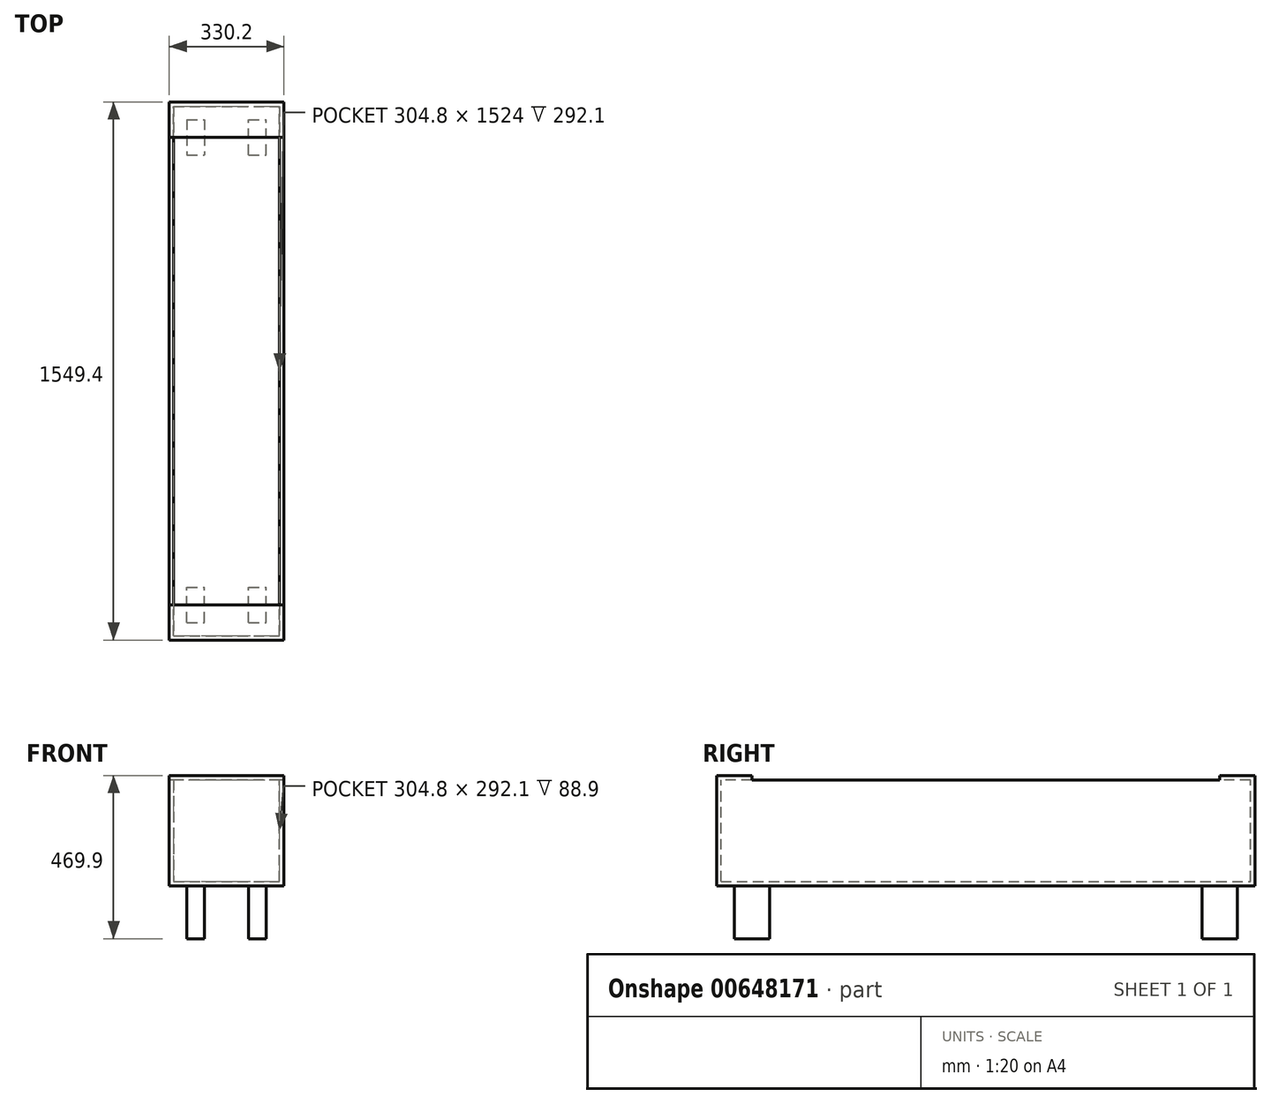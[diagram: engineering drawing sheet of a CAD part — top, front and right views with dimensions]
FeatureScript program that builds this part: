
annotation { "Feature Type Name" : "Feature", "Feature Type Description" : "" }
export const myFeature = defineFeature(function(context is Context, id is Id, definition is map)
    precondition{}
    {
        {
            var Q0;
            Q0=qCreatedBy(makeId("Front.planeOp"),FACE);
            var sketch = newSketch(context, id + "F0", { "sketchPlane" : qUnion([Q0])});
            skLineSegment(sketch, "E0.bottom", {"start": v(-260.83, -10.7) * mm, "end": v(43.97, -10.7) * mm});
            skLineSegment(sketch, "E0.top", {"start": v(-260.83, -23.4) * mm, "end": v(43.97, -23.4) * mm});
            skLineSegment(sketch, "E0.left", {"start": v(-260.83, -10.7) * mm, "end": v(-260.83, -23.4) * mm});
            skLineSegment(sketch, "E0.right", {"start": v(43.97, -10.7) * mm, "end": v(43.97, -23.4) * mm});
            skSolve(sketch);
        }
        {
            var Q0;
            Q0=makeQuery(id+"F0.imprint","IMPRINT",FACE,{"disambiguationData":[TD([[makeQuery(id+"F0.imprint","IMPRINT",EDGE,{"derivedFrom":sQuery(id+"F0.wireOp",EDGE,"E0.bottom")}),-1.0]])]});
            extrude(context, id + "F1", {"entities" : qUnion([Q0]), "depth" : 1524 * mm, "offsetDistance" : 25.4 * mm});
        }
        {
            var Q0;
            Q0=makeQuery(id+"F1.opExtrude","CAP_FACE",FACE,{"disambiguationData":[OSD([sQuery(id+"F0.wireOp",EDGE,"E0.bottom"),sQuery(id+"F0.wireOp",EDGE,"E0.top"),sQuery(id+"F0.wireOp",EDGE,"E0.left"),sQuery(id+"F0.wireOp",EDGE,"E0.right")])],"isStart":false});
            var sketch = newSketch(context, id + "F2", { "sketchPlane" : qUnion([Q0])});
            skLineSegment(sketch, "E1.bottom", {"start": v(43.97, -23.4) * mm, "end": v(56.67, -23.4) * mm});
            skLineSegment(sketch, "E1.top", {"start": v(43.97, 281.4) * mm, "end": v(56.67, 281.4) * mm});
            skLineSegment(sketch, "E1.left", {"start": v(43.97, -23.4) * mm, "end": v(43.97, 281.4) * mm});
            skLineSegment(sketch, "E1.right", {"start": v(56.67, -23.4) * mm, "end": v(56.67, 281.4) * mm});
            skLineSegment(sketch, "E2.bottom", {"start": v(-260.83, -23.4) * mm, "end": v(-273.53, -23.4) * mm});
            skLineSegment(sketch, "E2.top", {"start": v(-260.83, 281.4) * mm, "end": v(-273.53, 281.4) * mm});
            skLineSegment(sketch, "E2.left", {"start": v(-260.83, -23.4) * mm, "end": v(-260.83, 281.4) * mm});
            skLineSegment(sketch, "E2.right", {"start": v(-273.53, -23.4) * mm, "end": v(-273.53, 281.4) * mm});
            skSolve(sketch);
        }
        {
            var Q0;
            {var subQ3=sQuery(id+"F2.wireOp",EDGE,"E2.bottom");Q0=makeQuery(id+"F2.imprint","IMPRINT",FACE,{"disambiguationData":[TD([[makeQuery(id+"F2.imprint","IMPRINT",EDGE,{"derivedFrom":subQ3}),-1.0]])]});}
            var Q1;
            {var subQ2=sQuery(id+"F2.wireOp",EDGE,"E1.bottom");Q1=makeQuery(id+"F2.imprint","IMPRINT",FACE,{"disambiguationData":[TD([[makeQuery(id+"F2.imprint","IMPRINT",EDGE,{"derivedFrom":subQ2}),1.0]])]});}
            extrude(context, id + "F3", {"entities" : qUnion([Q0, Q1]), "operationType" : NewBodyOperationType.ADD, "oppositeDirection" : true, "depth" : 1524 * mm, "offsetDistance" : 25.4 * mm});
        }
        {
            var Q0;
            Q0=makeQuery(id+"F3.opExtrude","SWEPT_FACE",FACE,{"disambiguationData":[OSD([sQuery(id+"F2.wireOp",EDGE,"E2.right")])]});
            var sketch = newSketch(context, id + "F4", { "sketchPlane" : qUnion([Q0])});
            skLineSegment(sketch, "E3.bottom", {"start": v(0, -23.4) * mm, "end": v(-12.7, -23.4) * mm});
            skLineSegment(sketch, "E3.top", {"start": v(0, 281.4) * mm, "end": v(-12.7, 281.4) * mm});
            skLineSegment(sketch, "E3.left", {"start": v(0, -23.4) * mm, "end": v(0, 281.4) * mm});
            skLineSegment(sketch, "E3.right", {"start": v(-12.7, -23.4) * mm, "end": v(-12.7, 281.4) * mm});
            skLineSegment(sketch, "E4.bottom", {"start": v(1524, -23.4) * mm, "end": v(1536.7, -23.4) * mm});
            skLineSegment(sketch, "E4.top", {"start": v(1524, 281.4) * mm, "end": v(1536.7, 281.4) * mm});
            skLineSegment(sketch, "E4.left", {"start": v(1524, -23.4) * mm, "end": v(1524, 281.4) * mm});
            skLineSegment(sketch, "E4.right", {"start": v(1536.7, -23.4) * mm, "end": v(1536.7, 281.4) * mm});
            skSolve(sketch);
        }
        {
            var Q0;
            Q0=makeQuery(id+"F4.imprint","IMPRINT",FACE,{"disambiguationData":[TD([[makeQuery(id+"F4.imprint","IMPRINT",EDGE,{"derivedFrom":sQuery(id+"F4.wireOp",EDGE,"E3.bottom")}),-1.0]])]});
            var Q1;
            Q1=makeQuery(id+"F4.imprint","IMPRINT",FACE,{"disambiguationData":[TD([[makeQuery(id+"F4.imprint","IMPRINT",EDGE,{"derivedFrom":sQuery(id+"F4.wireOp",EDGE,"E4.bottom")}),1.0]])]});
            extrude(context, id + "F5", {"entities" : qUnion([Q0, Q1]), "operationType" : NewBodyOperationType.ADD, "oppositeDirection" : true, "depth" : 330.2 * mm, "offsetDistance" : 25.4 * mm});
        }
        {
            var Q0;
            Q0=makeQuery(id+"F5.boolean.opBoolean","MERGE",FACE,{"derivedFrom":[makeQuery(id+"F3.opExtrude","SWEPT_FACE",FACE,{"disambiguationData":[OSD([sQuery(id+"F2.wireOp",EDGE,"E2.right")])]}),makeQuery(id+"F5.opExtrude","CAP_FACE",FACE,{"disambiguationData":[OSD([sQuery(id+"F4.wireOp",EDGE,"E3.bottom"),sQuery(id+"F4.wireOp",EDGE,"E3.top"),sQuery(id+"F4.wireOp",EDGE,"E3.left"),sQuery(id+"F4.wireOp",EDGE,"E3.right")])],"isStart":true}),makeQuery(id+"F5.opExtrude","CAP_FACE",FACE,{"disambiguationData":[OSD([sQuery(id+"F4.wireOp",EDGE,"E4.bottom"),sQuery(id+"F4.wireOp",EDGE,"E4.top"),sQuery(id+"F4.wireOp",EDGE,"E4.left"),sQuery(id+"F4.wireOp",EDGE,"E4.right")])],"isStart":true})]});
            var sketch = newSketch(context, id + "F6", { "sketchPlane" : qUnion([Q0])});
            skLineSegment(sketch, "E5.bottom", {"start": v(-12.7, 281.4) * mm, "end": v(88.9, 281.4) * mm});
            skLineSegment(sketch, "E5.top", {"start": v(-12.7, 294.1) * mm, "end": v(88.9, 294.1) * mm});
            skLineSegment(sketch, "E5.left", {"start": v(-12.7, 281.4) * mm, "end": v(-12.7, 294.1) * mm});
            skLineSegment(sketch, "E5.right", {"start": v(88.9, 281.4) * mm, "end": v(88.9, 294.1) * mm});
            skLineSegment(sketch, "E6.bottom", {"start": v(1536.7, 281.4) * mm, "end": v(1435.1, 281.4) * mm});
            skLineSegment(sketch, "E6.top", {"start": v(1536.7, 294.1) * mm, "end": v(1435.1, 294.1) * mm});
            skLineSegment(sketch, "E6.left", {"start": v(1536.7, 281.4) * mm, "end": v(1536.7, 294.1) * mm});
            skLineSegment(sketch, "E6.right", {"start": v(1435.1, 281.4) * mm, "end": v(1435.1, 294.1) * mm});
            skSolve(sketch);
        }
        {
            var Q0;
            Q0=makeQuery(id+"F6.imprint","IMPRINT",FACE,{"disambiguationData":[TD([[makeQuery(id+"F6.imprint","IMPRINT",EDGE,{"derivedFrom":sQuery(id+"F6.wireOp",EDGE,"E6.bottom")}),1.0]])]});
            var Q1;
            Q1=makeQuery(id+"F6.imprint","IMPRINT",FACE,{"disambiguationData":[TD([[makeQuery(id+"F6.imprint","IMPRINT",EDGE,{"derivedFrom":sQuery(id+"F6.wireOp",EDGE,"E5.bottom")}),1.0]])]});
            extrude(context, id + "F7", {"entities" : qUnion([Q0, Q1]), "operationType" : NewBodyOperationType.ADD, "oppositeDirection" : true, "depth" : 330.2 * mm, "offsetDistance" : 25.4 * mm});
        }
        {
            var Q0;
            Q0=makeQuery(id+"F5.boolean.opBoolean","MERGE",FACE,{"derivedFrom":[makeQuery(id+"F3.boolean.opBoolean","MERGE",FACE,{"derivedFrom":[makeQuery(id+"F1.opExtrude","SWEPT_FACE",FACE,{"disambiguationData":[OSD([sQuery(id+"F0.wireOp",EDGE,"E0.top")])]}),makeQuery(id+"F3.opExtrude","SWEPT_FACE",FACE,{"disambiguationData":[OSD([sQuery(id+"F2.wireOp",EDGE,"E1.bottom")])]}),makeQuery(id+"F3.opExtrude","SWEPT_FACE",FACE,{"disambiguationData":[OSD([sQuery(id+"F2.wireOp",EDGE,"E2.bottom")])]})]}),makeQuery(id+"F5.opExtrude","SWEPT_FACE",FACE,{"disambiguationData":[OSD([sQuery(id+"F4.wireOp",EDGE,"E3.bottom")])]}),makeQuery(id+"F5.opExtrude","SWEPT_FACE",FACE,{"disambiguationData":[OSD([sQuery(id+"F4.wireOp",EDGE,"E4.bottom")])]})]});
            var sketch = newSketch(context, id + "F8", { "sketchPlane" : qUnion([Q0])});
            skLineSegment(sketch, "E7.bottom", {"start": v(-222.73, 1485.9) * mm, "end": v(-171.93, 1485.9) * mm});
            skLineSegment(sketch, "E7.top", {"start": v(-222.73, 1384.3) * mm, "end": v(-171.93, 1384.3) * mm});
            skLineSegment(sketch, "E7.left", {"start": v(-222.73, 1485.9) * mm, "end": v(-222.73, 1384.3) * mm});
            skLineSegment(sketch, "E7.right", {"start": v(-171.93, 1485.9) * mm, "end": v(-171.93, 1384.3) * mm});
            skLineSegment(sketch, "E8.bottom", {"start": v(-44.93, 1485.9) * mm, "end": v(5.87, 1485.9) * mm});
            skLineSegment(sketch, "E8.top", {"start": v(-44.93, 1384.3) * mm, "end": v(5.87, 1384.3) * mm});
            skLineSegment(sketch, "E8.left", {"start": v(-44.93, 1485.9) * mm, "end": v(-44.93, 1384.3) * mm});
            skLineSegment(sketch, "E8.right", {"start": v(5.87, 1485.9) * mm, "end": v(5.87, 1384.3) * mm});
            skLineSegment(sketch, "E9.bottom", {"start": v(-222.73, 38.1) * mm, "end": v(-171.93, 38.1) * mm});
            skLineSegment(sketch, "E9.top", {"start": v(-222.73, 139.7) * mm, "end": v(-171.93, 139.7) * mm});
            skLineSegment(sketch, "E9.left", {"start": v(-222.73, 38.1) * mm, "end": v(-222.73, 139.7) * mm});
            skLineSegment(sketch, "E9.right", {"start": v(-171.93, 38.1) * mm, "end": v(-171.93, 139.7) * mm});
            skLineSegment(sketch, "E10.bottom", {"start": v(-44.93, 139.7) * mm, "end": v(5.87, 139.7) * mm});
            skLineSegment(sketch, "E10.top", {"start": v(-44.93, 38.1) * mm, "end": v(5.87, 38.1) * mm});
            skLineSegment(sketch, "E10.left", {"start": v(-44.93, 139.7) * mm, "end": v(-44.93, 38.1) * mm});
            skLineSegment(sketch, "E10.right", {"start": v(5.87, 139.7) * mm, "end": v(5.87, 38.1) * mm});
            skSolve(sketch);
        }
        {
            var Q0;
            Q0=makeQuery(id+"F8.imprint","IMPRINT",FACE,{"disambiguationData":[TD([[makeQuery(id+"F8.imprint","IMPRINT",EDGE,{"derivedFrom":sQuery(id+"F8.wireOp",EDGE,"E9.bottom")}),1.0]])]});
            var Q1;
            Q1=makeQuery(id+"F8.imprint","IMPRINT",FACE,{"disambiguationData":[TD([[makeQuery(id+"F8.imprint","IMPRINT",EDGE,{"derivedFrom":sQuery(id+"F8.wireOp",EDGE,"E10.bottom")}),-1.0]])]});
            var Q2;
            Q2=makeQuery(id+"F8.imprint","IMPRINT",FACE,{"disambiguationData":[TD([[makeQuery(id+"F8.imprint","IMPRINT",EDGE,{"derivedFrom":sQuery(id+"F8.wireOp",EDGE,"E7.bottom")}),-1.0]])]});
            var Q3;
            Q3=makeQuery(id+"F8.imprint","IMPRINT",FACE,{"disambiguationData":[TD([[makeQuery(id+"F8.imprint","IMPRINT",EDGE,{"derivedFrom":sQuery(id+"F8.wireOp",EDGE,"E8.bottom")}),-1.0]])]});
            extrude(context, id + "F9", {"entities" : qUnion([Q0, Q1, Q2, Q3]), "operationType" : NewBodyOperationType.ADD, "depth" : 152.4 * mm, "offsetDistance" : 25.4 * mm});
        }
    });
